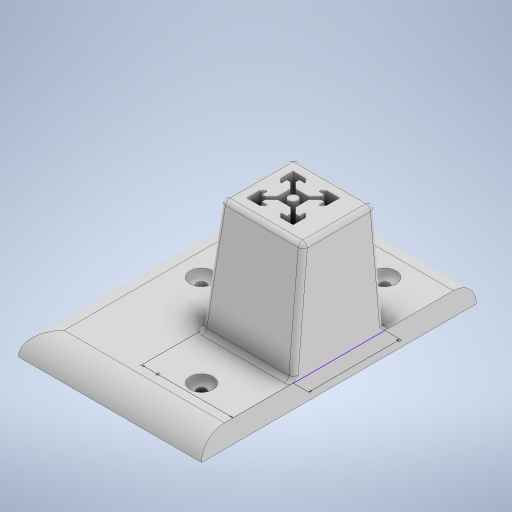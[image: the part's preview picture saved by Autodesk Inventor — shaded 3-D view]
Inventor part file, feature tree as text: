
AUTODESK INVENTOR PART (.ipt)
format: ipt  version: 2023 (Build 270158000, 158)  size: 427,008 bytes
history: native  units: mm
features: sketch x10, extrude x4, fillet x4, chamfer x3
ambient origin geometry x8: Origin, YZ Plane, XZ Plane, XY Plane, X Axis, Y Axis, Z Axis, Center Point
bodies: Body1 (feature_tree)
feature tree (21):
  sketch  "Szkic1"
  sketch  "Szkic2"
  sketch  "Szkic3"
  sketch  "Szkic4"
  sketch  "Szkic5"
  sketch  "Szkic6"
  sketch  "Szkic8"
  extrude  "Wyciągnięcie proste2"  Depth=40.0mm
  extrude  "Wyciągnięcie proste3"  Depth=40.0mm
  sketch  "Szkic11"
  extrude  "Wyciągnięcie proste6"  Depth=40.0mm
  extrude  "Wyciągnięcie proste7"  Depth=50.0mm TaperAngle=0.0deg
  fillet  "Zaokrąglenie3"  Radius=50.0mm
  chamfer  "Faza1"  Distance=40.0mm
  chamfer  "Faza2"  Distance=40.0mm
  chamfer  "Faza3"  Distance=40.0mm
  fillet  "Zaokrąglenie5"  Radius=10.0mm
  fillet  "Zaokrąglenie6"  Radius=5.0mm
  fillet  "Zaokrąglenie7"  Radius=5.0mm
  sketch  "Szkic12"
  sketch  "Szkic14"
